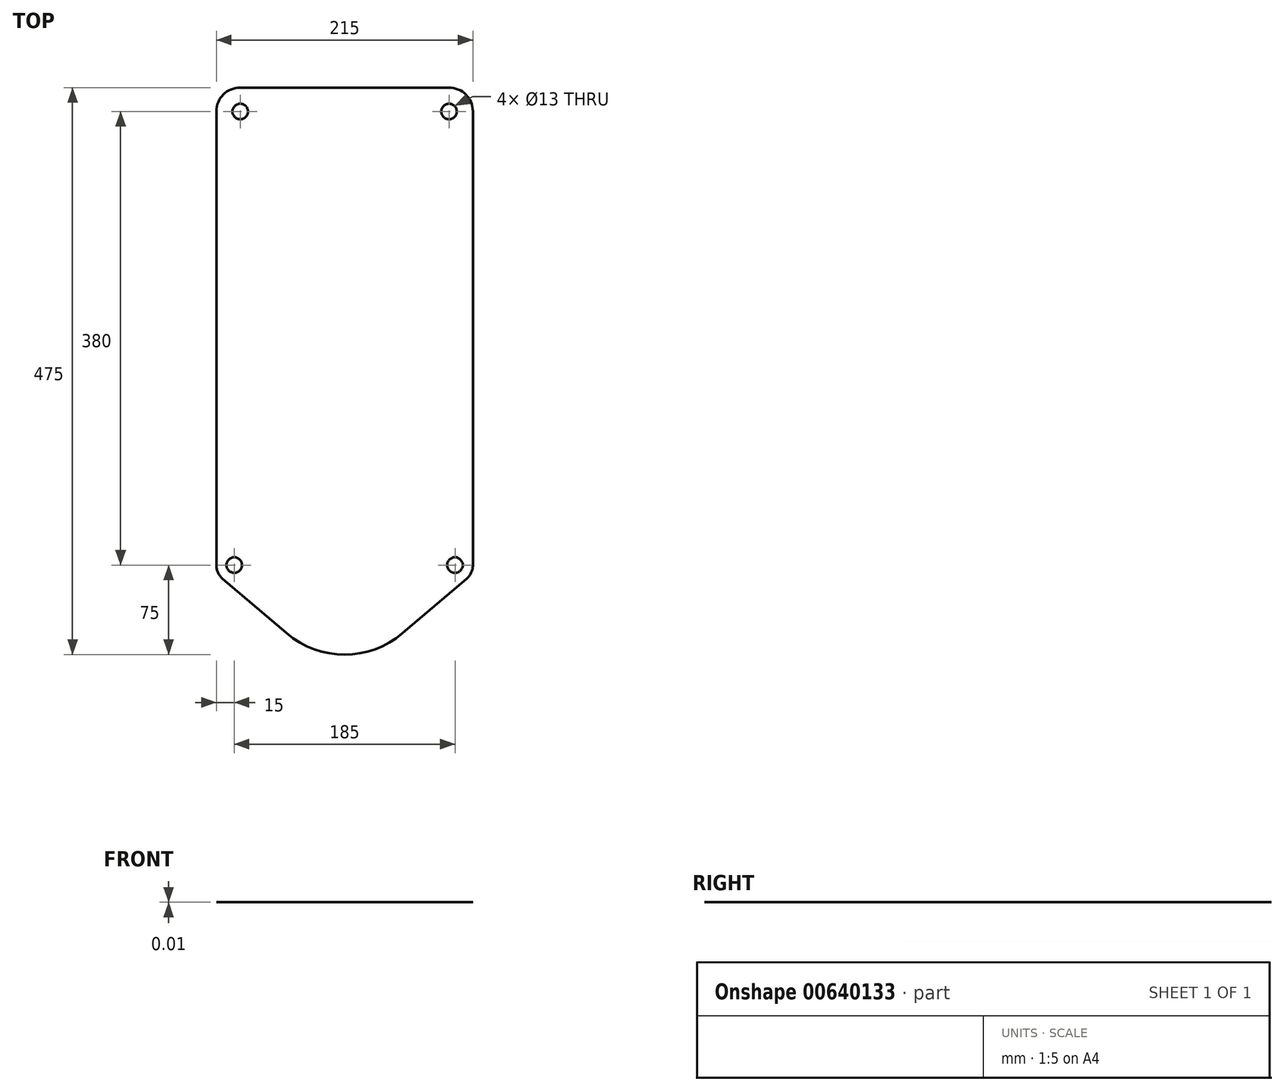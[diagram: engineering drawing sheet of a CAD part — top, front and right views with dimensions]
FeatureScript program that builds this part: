
annotation { "Feature Type Name" : "Feature", "Feature Type Description" : "" }
export const myFeature = defineFeature(function(context is Context, id is Id, definition is map)
    precondition{}
    {
        {
            var Q0;
            Q0=qCreatedBy(makeId("Top.planeOp"),FACE);
            var sketch = newSketch(context, id + "F0", { "sketchPlane" : qUnion([Q0])});
            skCircle(sketch, "E0", {"center": v(0, 0) * mm, "radius": 75 * mm});
            skCircle(sketch, "E1", {"center": v(92.5, 0) * mm, "radius": 6.5 * mm});
            skCircle(sketch, "E2", {"center": v(-92.5, 0) * mm, "radius": 6.5 * mm});
            skCircle(sketch, "E3", {"center": v(-92.5, 0) * mm, "radius": 15 * mm});
            skCircle(sketch, "E4", {"center": v(92.5, 0) * mm, "radius": 15 * mm});
            skLineSegment(sketch, "E5", {"start": v(-102.23, 11.42) * mm, "end": v(-48.65, 57.08) * mm});
            skLineSegment(sketch, "E6", {"start": v(102.23, 11.42) * mm, "end": v(48.65, 57.08) * mm});
            skLineSegment(sketch, "E7", {"start": v(102.23, -11.42) * mm, "end": v(48.65, -57.08) * mm});
            skLineSegment(sketch, "E8", {"start": v(-102.23, -11.42) * mm, "end": v(-48.65, -57.08) * mm});
            skLineSegment(sketch, "E9", {"start": v(-107.5, 0) * mm, "end": v(-107.5, 20.74) * mm, "construction": true});
            skLineSegment(sketch, "E10", {"start": v(107.5, 0) * mm, "end": v(107.5, 25.69) * mm, "construction": true});
            skLineSegment(sketch, "E11", {"start": v(0, 0) * mm, "end": v(0, 31.78) * mm, "construction": true});
            skLineSegment(sketch, "E12.bottom", {"start": v(0, 75) * mm, "end": v(180, 75) * mm});
            skLineSegment(sketch, "E12.top", {"start": v(0, -75) * mm, "end": v(180, -75) * mm});
            skLineSegment(sketch, "E12.left", {"start": v(0, 75) * mm, "end": v(0, -75) * mm});
            skLineSegment(sketch, "E12.right", {"start": v(200, 55) * mm, "end": v(200, -55) * mm});
            skPoint(sketch, "E12.middle", {"position": v(100, 0) * mm});
            skPoint(sketch, "E13.visualSharp", {"position": v(200, 75) * mm});
            skArc(sketch, "E13.filletArc", {"start": v(200, 55) * mm, "mid": v(194.14, 69.14) * mm, "end": v(180, 75) * mm});
            skPoint(sketch, "E14.visualSharp", {"position": v(200, -75) * mm});
            skArc(sketch, "E14.filletArc", {"start": v(180, -75) * mm, "mid": v(194.14, -69.14) * mm, "end": v(200, -55) * mm});
            skCircle(sketch, "E15", {"center": v(180, 55) * mm, "radius": 6.5 * mm});
            skCircle(sketch, "E16", {"center": v(180, -55) * mm, "radius": 6.5 * mm});
            skLineSegment(sketch, "E17.bottom", {"start": v(-107.5, 0) * mm, "end": v(107.5, 0) * mm});
            skLineSegment(sketch, "E17.top", {"start": v(-87.5, 400) * mm, "end": v(87.5, 400) * mm});
            skLineSegment(sketch, "E17.left", {"start": v(-107.5, 0) * mm, "end": v(-107.5, 380) * mm});
            skLineSegment(sketch, "E17.right", {"start": v(107.5, 0) * mm, "end": v(107.5, 380) * mm});
            skPoint(sketch, "E18.visualSharp", {"position": v(-107.5, 400) * mm});
            skArc(sketch, "E18.filletArc", {"start": v(-87.5, 400) * mm, "mid": v(-101.64, 394.14) * mm, "end": v(-107.5, 380) * mm});
            skPoint(sketch, "E19.visualSharp", {"position": v(107.5, 400) * mm});
            skArc(sketch, "E19.filletArc", {"start": v(107.5, 380) * mm, "mid": v(101.64, 394.14) * mm, "end": v(87.5, 400) * mm});
            skCircle(sketch, "E20", {"center": v(-87.5, 380) * mm, "radius": 6.5 * mm});
            skCircle(sketch, "E21", {"center": v(87.5, 380) * mm, "radius": 6.5 * mm});
            skSolve(sketch);
        }
        {
            var Q0;
            {var subQ0=sQuery(id+"F0.wireOp",EDGE,"E0");var subQ1=makeQuery(id+"F0.imprint","INTERSECT",VERTEX,{"derivedFrom":[subQ0,sQuery(id+"F0.wireOp",EDGE,"E8")]});Q0=makeQuery(id+"F0.imprint","IMPRINT",FACE,{"disambiguationData":[TD([[makeQuery(id+"F0.imprint","IMPRINT",EDGE,{"disambiguationData":[TD([[subQ1,1.0]])],"derivedFrom":subQ0}),1.0]])]});}
            var Q1;
            {var subQ0=sQuery(id+"F0.wireOp",EDGE,"E8");Q1=makeQuery(id+"F0.imprint","IMPRINT",FACE,{"disambiguationData":[TD([[makeQuery(id+"F0.imprint","IMPRINT",EDGE,{"derivedFrom":subQ0}),1.0]])]});}
            var Q2;
            {var subQ2=sQuery(id+"F0.wireOp",EDGE,"E17.bottom");var subQ5=sQuery(id+"F0.wireOp",EDGE,"E2");var subQ6=makeQuery(id+"F0.imprint","INTERSECT",VERTEX,{"disambiguationData":[OD(0.0)],"derivedFrom":[subQ5,subQ2]});Q2=makeQuery(id+"F0.imprint","IMPRINT",FACE,{"disambiguationData":[TD([[makeQuery(id+"F0.imprint","IMPRINT",EDGE,{"disambiguationData":[TD([[subQ6,-1.0]])],"derivedFrom":subQ5}),-1.0]])]});}
            var Q3;
            {var subQ0=sQuery(id+"F0.wireOp",EDGE,"E0");var subQ1=makeQuery(id+"F0.imprint","INTERSECT",VERTEX,{"derivedFrom":[subQ0,sQuery(id+"F0.wireOp",EDGE,"E7")]});Q3=makeQuery(id+"F0.imprint","IMPRINT",FACE,{"disambiguationData":[TD([[makeQuery(id+"F0.imprint","IMPRINT",EDGE,{"disambiguationData":[TD([[subQ1,-1.0]])],"derivedFrom":subQ0}),1.0]])]});}
            var Q4;
            {var subQ0=sQuery(id+"F0.wireOp",EDGE,"E17.bottom");var subQ3=sQuery(id+"F0.wireOp",EDGE,"E2");var subQ4=makeQuery(id+"F0.imprint","INTERSECT",VERTEX,{"disambiguationData":[OD(0.0)],"derivedFrom":[subQ3,subQ0]});Q4=makeQuery(id+"F0.imprint","IMPRINT",FACE,{"disambiguationData":[TD([[makeQuery(id+"F0.imprint","IMPRINT",EDGE,{"disambiguationData":[TD([[subQ4,1.0]])],"derivedFrom":subQ3}),-1.0]])]});}
            var Q5;
            {var subQ7=sQuery(id+"F0.wireOp",EDGE,"E6");Q5=makeQuery(id+"F0.imprint","IMPRINT",FACE,{"disambiguationData":[TD([[makeQuery(id+"F0.imprint","IMPRINT",EDGE,{"derivedFrom":subQ7}),-1.0]])]});}
            var Q6;
            {var subQ1=sQuery(id+"F0.wireOp",EDGE,"E5");Q6=makeQuery(id+"F0.imprint","IMPRINT",FACE,{"disambiguationData":[TD([[makeQuery(id+"F0.imprint","IMPRINT",EDGE,{"derivedFrom":subQ1}),1.0]])]});}
            var Q7;
            {var subQ2=sQuery(id+"F0.wireOp",EDGE,"E17.bottom");var subQ4=sQuery(id+"F0.wireOp",EDGE,"E1");var subQ5=makeQuery(id+"F0.imprint","INTERSECT",VERTEX,{"disambiguationData":[OD(0.0)],"derivedFrom":[subQ4,subQ2]});Q7=makeQuery(id+"F0.imprint","IMPRINT",FACE,{"disambiguationData":[TD([[makeQuery(id+"F0.imprint","IMPRINT",EDGE,{"disambiguationData":[TD([[subQ5,1.0]])],"derivedFrom":subQ4}),-1.0]])]});}
            var Q8;
            {var subQ0=sQuery(id+"F0.wireOp",EDGE,"E17.bottom");var subQ1=sQuery(id+"F0.wireOp",EDGE,"E1");var subQ2=makeQuery(id+"F0.imprint","INTERSECT",VERTEX,{"disambiguationData":[OD(0.0)],"derivedFrom":[subQ1,subQ0]});Q8=makeQuery(id+"F0.imprint","IMPRINT",FACE,{"disambiguationData":[TD([[makeQuery(id+"F0.imprint","IMPRINT",EDGE,{"disambiguationData":[TD([[subQ2,-1.0]])],"derivedFrom":subQ1}),-1.0]])]});}
            var Q9;
            {var subQ0=sQuery(id+"F0.wireOp",EDGE,"E6");Q9=makeQuery(id+"F0.imprint","IMPRINT",FACE,{"disambiguationData":[TD([[makeQuery(id+"F0.imprint","IMPRINT",EDGE,{"derivedFrom":subQ0}),1.0]])]});}
            var Q10;
            {var subQ0=sQuery(id+"F0.wireOp",EDGE,"E7");Q10=makeQuery(id+"F0.imprint","IMPRINT",FACE,{"disambiguationData":[TD([[makeQuery(id+"F0.imprint","IMPRINT",EDGE,{"derivedFrom":subQ0}),-1.0]])]});}
            var Q11;
            {var subQ0=sQuery(id+"F0.wireOp",EDGE,"E0");var subQ1=makeQuery(id+"F0.imprint","INTERSECT",VERTEX,{"derivedFrom":[subQ0,sQuery(id+"F0.wireOp",EDGE,"E6")]});Q11=makeQuery(id+"F0.imprint","IMPRINT",FACE,{"disambiguationData":[TD([[makeQuery(id+"F0.imprint","IMPRINT",EDGE,{"disambiguationData":[TD([[subQ1,1.0]])],"derivedFrom":subQ0}),1.0]])]});}
            var Q12;
            {var subQ0=sQuery(id+"F0.wireOp",EDGE,"E5");Q12=makeQuery(id+"F0.imprint","IMPRINT",FACE,{"disambiguationData":[TD([[makeQuery(id+"F0.imprint","IMPRINT",EDGE,{"derivedFrom":subQ0}),-1.0]])]});}
            var Q13;
            {var subQ0=sQuery(id+"F0.wireOp",EDGE,"E0");var subQ1=makeQuery(id+"F0.imprint","INTERSECT",VERTEX,{"derivedFrom":[subQ0,sQuery(id+"F0.wireOp",EDGE,"E5")]});Q13=makeQuery(id+"F0.imprint","IMPRINT",FACE,{"disambiguationData":[TD([[makeQuery(id+"F0.imprint","IMPRINT",EDGE,{"disambiguationData":[TD([[subQ1,-1.0]])],"derivedFrom":subQ0}),1.0]])]});}
            extrude(context, id + "F1", {"entities" : qUnion([Q0, Q1, Q2, Q3, Q4, Q5, Q6, Q7, Q8, Q9, Q10, Q11, Q12, Q13]), "depth" : 1 / 101.6 * mm, "offsetDistance" : 25 * mm});
        }
    });
